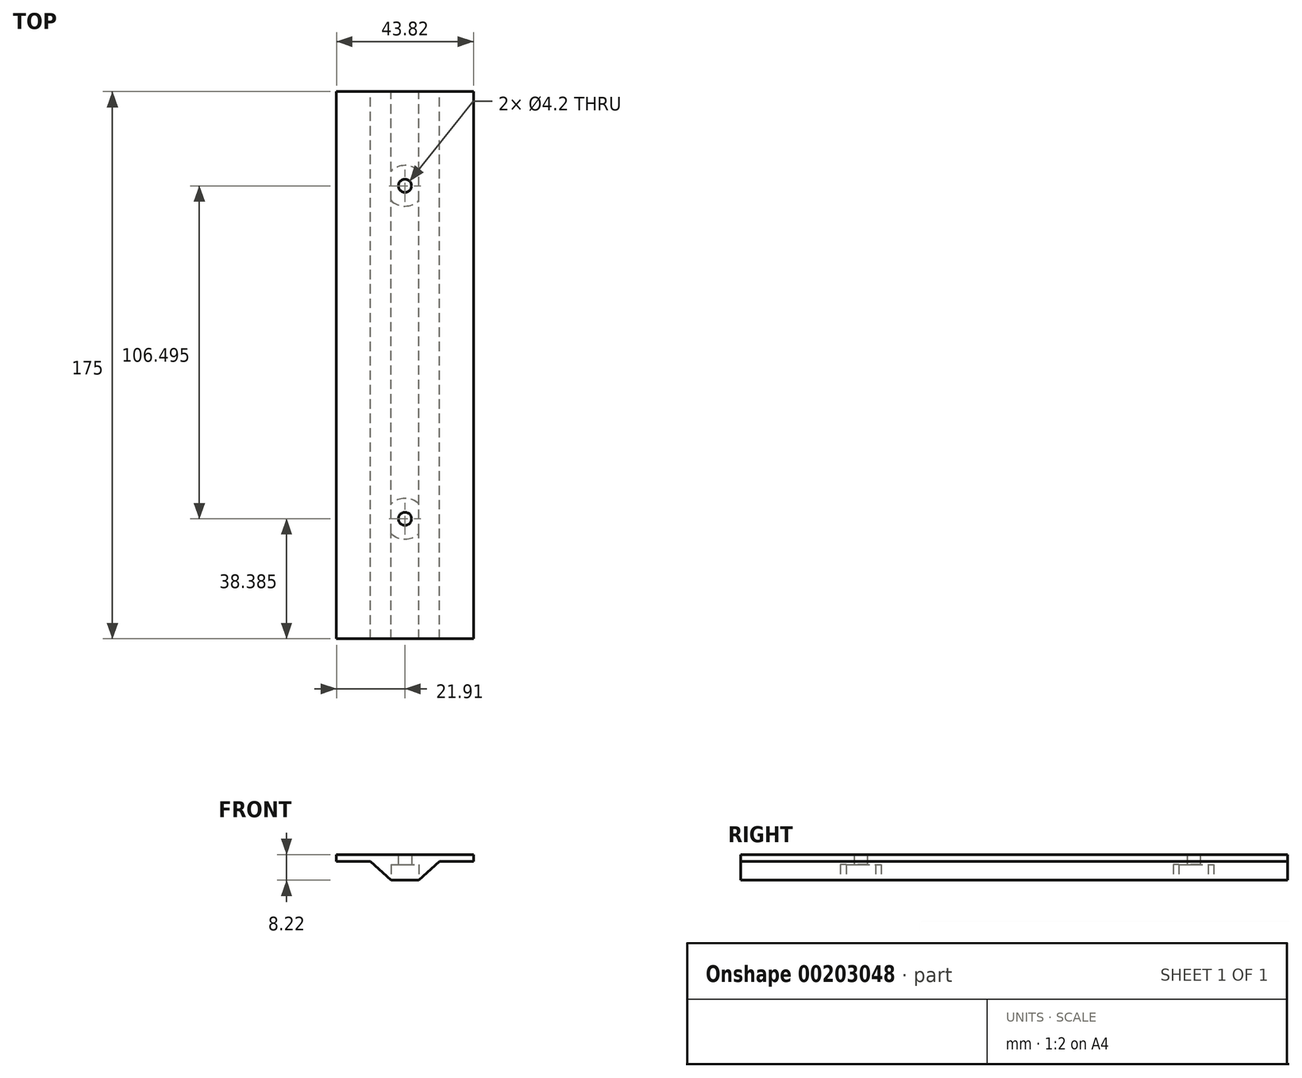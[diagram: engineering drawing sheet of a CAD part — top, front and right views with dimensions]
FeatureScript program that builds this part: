
annotation { "Feature Type Name" : "Feature", "Feature Type Description" : "" }
export const myFeature = defineFeature(function(context is Context, id is Id, definition is map)
    precondition{}
    {
        {
            var Q0;
            Q0=qCreatedBy(makeId("Front.planeOp"),FACE);
            var sketch = newSketch(context, id + "F0", { "sketchPlane" : qUnion([Q0])});
            skLineSegment(sketch, "E0.bottom", {"start": v(21.91, 10) * mm, "end": v(11, 10) * mm, "construction": true});
            skLineSegment(sketch, "E1.top", {"start": v(0, 4) * mm, "end": v(4.5, 4) * mm, "construction": true});
            skLineSegment(sketch, "E2", {"start": v(21.91, 10) * mm, "end": v(11, 10) * mm});
            skLineSegment(sketch, "E3", {"start": v(11, 10) * mm, "end": v(4.5, 4) * mm});
            skLineSegment(sketch, "E4", {"start": v(4.5, 4) * mm, "end": v(0, 4) * mm});
            skLineSegment(sketch, "E5.MirrorCS", {"start": v(-21.91, 10) * mm, "end": v(-11, 10) * mm, "construction": true});
            skLineSegment(sketch, "E6.MirrorCS", {"start": v(-21.91, 10) * mm, "end": v(-11, 10) * mm});
            skLineSegment(sketch, "E7.MirrorCS", {"start": v(0, 4) * mm, "end": v(-4.5, 4) * mm, "construction": true});
            skLineSegment(sketch, "E8.MirrorCS", {"start": v(-4.5, 4) * mm, "end": v(0, 4) * mm});
            skLineSegment(sketch, "E9.MirrorCS", {"start": v(-11, 10) * mm, "end": v(-4.5, 4) * mm});
            skLineSegment(sketch, "E10.bottom", {"start": v(-21.91, 10) * mm, "end": v(21.91, 10) * mm});
            skLineSegment(sketch, "E10.top", {"start": v(-21.91, 12.22) * mm, "end": v(21.91, 12.22) * mm});
            skLineSegment(sketch, "E10.left", {"start": v(-21.91, 10) * mm, "end": v(-21.91, 12.22) * mm});
            skLineSegment(sketch, "E10.right", {"start": v(21.91, 10) * mm, "end": v(21.91, 12.22) * mm});
            skSolve(sketch);
        }
        {
            var Q0;
            {var subQ1=sQuery(id+"F0.wireOp",EDGE,"E3");Q0=makeQuery(id+"F0.imprint","IMPRINT",FACE,{"disambiguationData":[TD([[makeQuery(id+"F0.imprint","IMPRINT",EDGE,{"derivedFrom":subQ1}),-1.0]])]});}
            var Q1;
            Q1=makeQuery(id+"F0.imprint","IMPRINT",FACE,{"disambiguationData":[TD([[makeQuery(id+"F0.imprint","IMPRINT",EDGE,{"derivedFrom":sQuery(id+"F0.wireOp",EDGE,"E10.top")}),-1.0]])]});
            extrude(context, id + "F1", {"entities" : qUnion([Q0, Q1]), "depth" : 175 * mm});
        }
        {
            var Q0;
            Q0=makeQuery(id+"F1.opExtrude","SWEPT_FACE",FACE,{"disambiguationData":[OSD([sQuery(id+"F0.wireOp",EDGE,"E4"),sQuery(id+"F0.wireOp",EDGE,"E8.MirrorCS")])]});
            var sketch = newSketch(context, id + "F2", { "sketchPlane" : qUnion([Q0])});
            skCircle(sketch, "E11", {"center": v(0, 30.12) * mm, "radius": 2.1 * mm});
            skCircle(sketch, "E12", {"center": v(0, 30.12) * mm, "radius": 6.5 * mm});
            skCircle(sketch, "E13", {"center": v(0, 136.62) * mm, "radius": 2.1 * mm});
            skCircle(sketch, "E14", {"center": v(0, 136.62) * mm, "radius": 6.5 * mm});
            skSolve(sketch);
        }
        {
            var Q0;
            Q0=makeQuery(id+"F2.imprint","IMPRINT",FACE,{"disambiguationData":[TD([[makeQuery(id+"F2.imprint","IMPRINT",EDGE,{"derivedFrom":sQuery(id+"F2.wireOp",EDGE,"E13")}),1.0]])]});
            var Q1;
            Q1=sQuery(id+"F2.wireOp",EDGE,"E13");
            var Q2;
            Q2=sQuery(id+"F2.wireOp",EDGE,"E11");
            extrude(context, id + "F3", {"entities" : qUnion([Q0]), "operationType" : NewBodyOperationType.REMOVE, "surfaceEntities" : qUnion([Q1, Q2]), "oppositeDirection" : true, "depth" : 25 * mm});
        }
        {
            var Q0;
            Q0=makeQuery(id+"F2.imprint","IMPRINT",FACE,{"disambiguationData":[TD([[makeQuery(id+"F2.imprint","IMPRINT",EDGE,{"derivedFrom":sQuery(id+"F2.wireOp",EDGE,"E11")}),1.0]])]});
            extrude(context, id + "F4", {"entities" : qUnion([Q0]), "operationType" : NewBodyOperationType.REMOVE, "oppositeDirection" : true, "depth" : 25 * mm});
        }
        {
            var Q0;
            {var subQ0=sQuery(id+"F2.wireOp",EDGE,"E12");var subQ1=makeQuery(id+"F1.opExtrude","SWEPT_EDGE",EDGE,{"disambiguationData":[OSD([sQuery(id+"F0.wireOp",EDGE,"E8.MirrorCS"),sQuery(id+"F0.wireOp",EDGE,"E9.MirrorCS")])]});var subQ2=makeQuery(id+"F2.imprint","INTERSECT",VERTEX,{"disambiguationData":[OD(0.0)],"derivedFrom":[subQ1,subQ0]});Q0=makeQuery(id+"F2.imprint","IMPRINT",FACE,{"disambiguationData":[TD([[makeQuery(id+"F2.imprint","IMPRINT",EDGE,{"disambiguationData":[TD([[subQ2,-1.0]])],"derivedFrom":subQ0}),1.0]])]});}
            var Q1;
            {var subQ0=sQuery(id+"F2.wireOp",EDGE,"E12");var subQ1=makeQuery(id+"F1.opExtrude","SWEPT_EDGE",EDGE,{"disambiguationData":[OSD([sQuery(id+"F0.wireOp",EDGE,"E3"),sQuery(id+"F0.wireOp",EDGE,"E4")])]});var subQ2=makeQuery(id+"F2.imprint","INTERSECT",VERTEX,{"disambiguationData":[OD(0.0)],"derivedFrom":[subQ1,subQ0]});Q1=makeQuery(id+"F2.imprint","IMPRINT",FACE,{"disambiguationData":[TD([[makeQuery(id+"F2.imprint","IMPRINT",EDGE,{"disambiguationData":[TD([[subQ2,1.0]])],"derivedFrom":subQ0}),1.0]])]});}
            var Q2;
            Q2=makeQuery(id+"F2.imprint","IMPRINT",FACE,{"disambiguationData":[TD([[makeQuery(id+"F2.imprint","IMPRINT",EDGE,{"derivedFrom":sQuery(id+"F2.wireOp",EDGE,"E11")}),-1.0]])]});
            extrude(context, id + "F5", {"entities" : qUnion([Q0, Q1, Q2]), "operationType" : NewBodyOperationType.REMOVE, "oppositeDirection" : true, "depth" : 5 * mm});
        }
        {
            var Q0;
            {var subQ0=sQuery(id+"F2.wireOp",EDGE,"E14");var subQ1=makeQuery(id+"F1.opExtrude","SWEPT_EDGE",EDGE,{"disambiguationData":[OSD([sQuery(id+"F0.wireOp",EDGE,"E8.MirrorCS"),sQuery(id+"F0.wireOp",EDGE,"E9.MirrorCS")])]});var subQ2=makeQuery(id+"F2.imprint","INTERSECT",VERTEX,{"disambiguationData":[OD(0.0)],"derivedFrom":[subQ1,subQ0]});Q0=makeQuery(id+"F2.imprint","IMPRINT",FACE,{"disambiguationData":[TD([[makeQuery(id+"F2.imprint","IMPRINT",EDGE,{"disambiguationData":[TD([[subQ2,-1.0]])],"derivedFrom":subQ0}),1.0]])]});}
            var Q1;
            {var subQ0=sQuery(id+"F2.wireOp",EDGE,"E14");var subQ1=makeQuery(id+"F1.opExtrude","SWEPT_EDGE",EDGE,{"disambiguationData":[OSD([sQuery(id+"F0.wireOp",EDGE,"E3"),sQuery(id+"F0.wireOp",EDGE,"E4")])]});var subQ2=makeQuery(id+"F2.imprint","INTERSECT",VERTEX,{"disambiguationData":[OD(0.0)],"derivedFrom":[subQ1,subQ0]});Q1=makeQuery(id+"F2.imprint","IMPRINT",FACE,{"disambiguationData":[TD([[makeQuery(id+"F2.imprint","IMPRINT",EDGE,{"disambiguationData":[TD([[subQ2,1.0]])],"derivedFrom":subQ0}),1.0]])]});}
            var Q2;
            Q2=makeQuery(id+"F2.imprint","IMPRINT",FACE,{"disambiguationData":[TD([[makeQuery(id+"F2.imprint","IMPRINT",EDGE,{"derivedFrom":sQuery(id+"F2.wireOp",EDGE,"E13")}),-1.0]])]});
            extrude(context, id + "F6", {"entities" : qUnion([Q0, Q1, Q2]), "operationType" : NewBodyOperationType.REMOVE, "oppositeDirection" : true, "depth" : 5 * mm});
        }
    });
